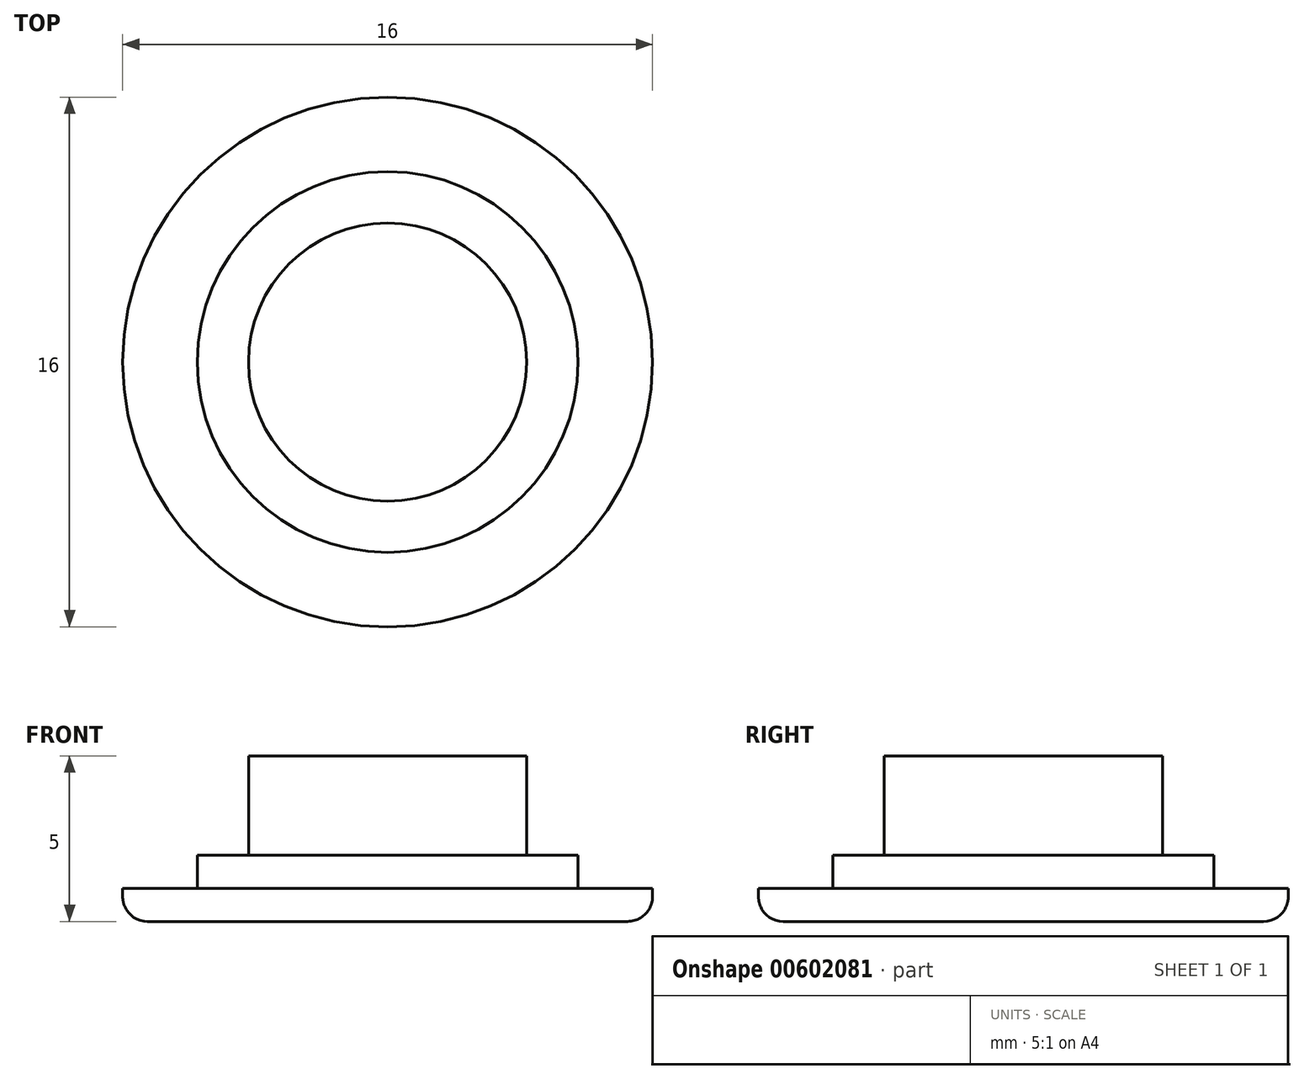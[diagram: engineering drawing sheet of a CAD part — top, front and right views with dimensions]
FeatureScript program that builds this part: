
annotation { "Feature Type Name" : "Feature", "Feature Type Description" : "" }
export const myFeature = defineFeature(function(context is Context, id is Id, definition is map)
    precondition{}
    {
        {
            var Q0;
            Q0=qCreatedBy(makeId("Top.planeOp"),FACE);
            var sketch = newSketch(context, id + "F0", { "sketchPlane" : qUnion([Q0])});
            skCircle(sketch, "E0", {"center": v(0, 0) * mm, "radius": 8 * mm});
            skSolve(sketch);
        }
        {
            var Q0;
            Q0=makeQuery(id+"F0.imprint","IMPRINT",FACE,{"disambiguationData":[TD([[makeQuery(id+"F0.imprint","IMPRINT",EDGE,{"derivedFrom":sQuery(id+"F0.wireOp",EDGE,"E0")}),1.0]])]});
            extrude(context, id + "F1", {"entities" : qUnion([Q0]), "depth" : 1 * mm});
        }
        {
            var Q0;
            Q0=makeQuery(id+"F1.opExtrude","CAP_FACE",FACE,{"disambiguationData":[OSD([sQuery(id+"F0.wireOp",EDGE,"E0")])],"isStart":false});
            var sketch = newSketch(context, id + "F2", { "sketchPlane" : qUnion([Q0])});
            skCircle(sketch, "E1", {"center": v(0, 0) * mm, "radius": 5.75 * mm});
            skSolve(sketch);
        }
        {
            var Q0;
            Q0=makeQuery(id+"F2.imprint","IMPRINT",FACE,{"disambiguationData":[TD([[makeQuery(id+"F2.imprint","IMPRINT",EDGE,{"derivedFrom":sQuery(id+"F2.wireOp",EDGE,"E1")}),1.0]])]});
            extrude(context, id + "F3", {"entities" : qUnion([Q0]), "operationType" : NewBodyOperationType.ADD, "depth" : 1 * mm});
        }
        {
            var Q0;
            Q0=makeQuery(id+"F3.opExtrude","CAP_FACE",FACE,{"disambiguationData":[OSD([sQuery(id+"F2.wireOp",EDGE,"E1")])],"isStart":false});
            var sketch = newSketch(context, id + "F4", { "sketchPlane" : qUnion([Q0])});
            skCircle(sketch, "E2", {"center": v(0, 0) * mm, "radius": 4.2 * mm});
            skSolve(sketch);
        }
        {
            var Q0;
            Q0=makeQuery(id+"F4.imprint","IMPRINT",FACE,{"disambiguationData":[TD([[makeQuery(id+"F4.imprint","IMPRINT",EDGE,{"derivedFrom":sQuery(id+"F4.wireOp",EDGE,"E2")}),1.0]])]});
            extrude(context, id + "F5", {"entities" : qUnion([Q0]), "operationType" : NewBodyOperationType.ADD, "depth" : 3 * mm});
        }
        {
            var Q0;
            Q0=makeQuery(id+"F1.opExtrude","CAP_EDGE",EDGE,{"disambiguationData":[OSD([sQuery(id+"F0.wireOp",EDGE,"E0")])],"isStart":true});
            fillet(context, id + "F6", {"entities" : qUnion([Q0]), "radius" : .75 * mm, "tangentPropagation" : true, "allowEdgeOverflow" : false});
        }
    });
